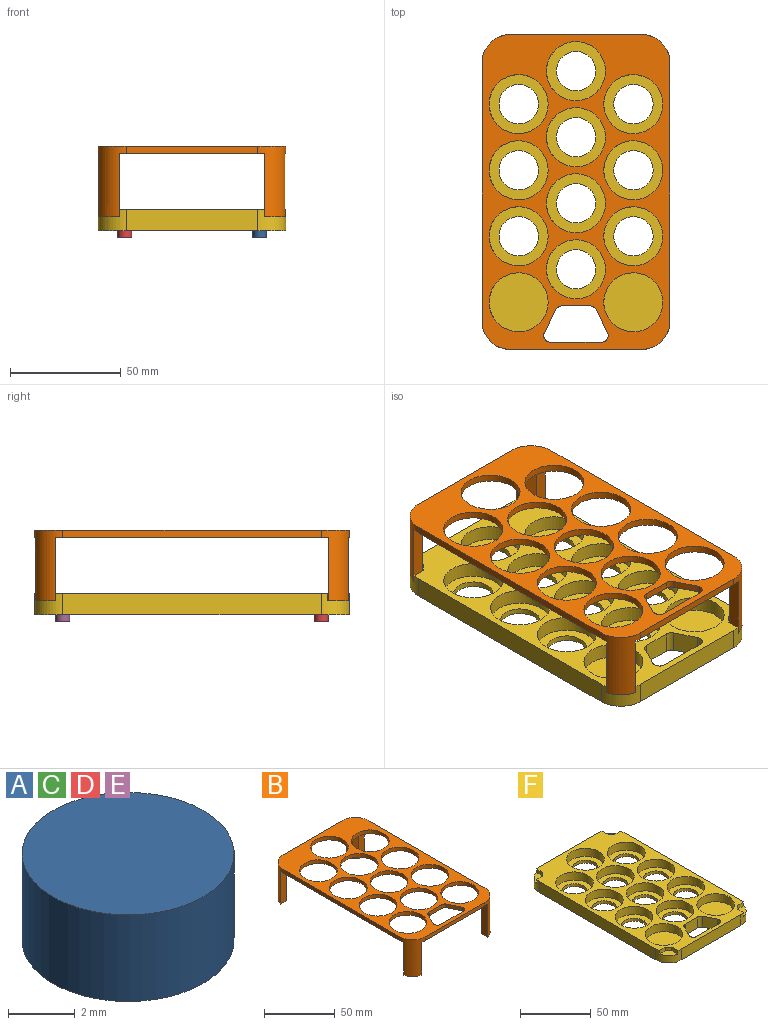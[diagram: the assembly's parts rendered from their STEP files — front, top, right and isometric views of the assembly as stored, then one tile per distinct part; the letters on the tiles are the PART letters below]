
ASSEMBLY  parts=6 mates=5
PART A: 3 faces, bbox 6.4x6.4x3.2 mm
  f0: cylinder r=3.17mm len=6.35mm, axis (0,0,-1), area 63.3mm2, adj f1,f2
  f1: plane 6.35x6.35mm, normal (0,0,1), area 31.7mm2, adj f0
  f2: plane 6.35x6.35mm, normal (0,0,-1), area 31.7mm2, adj f0
PART B: 46 faces, bbox 84.8x142.2x31.8 mm
  f0: plane 142.24x84.84mm, normal (0,0,-1), area 4623.7mm2, adj f4,f5,f6,f8,f9,f11,f12,f13
  f1: plane 142.24x84.84mm, normal (0,0,1), area 4829.7mm2, adj f4,f11,f12,f13,f18,f19,f20,f21
  f2: plane 9.12x9.12mm, normal (0,0,-1), area 51.5mm2, adj f8,f17,f39,f42
  f3: plane 9.12x9.12mm, normal (0,0,-1), area 51.5mm2, adj f9,f14,f38,f43
  f4: plane 116.84x3.18mm, normal (-1,0,0), area 371mm2, adj f0,f1,f39,f41
  f5: plane 28.58x5.82mm, normal (1,0,0), area 166.3mm2, adj f0,f7,f41,f44
  f6: plane 28.58x5.82mm, normal (-1,0,0), area 166.3mm2, adj f0,f10,f40,f45
  f7: plane 9.12x9.12mm, normal (0,0,-1), area 51.5mm2, adj f5,f16,f41,f44
  f8: plane 28.58x5.82mm, normal (1,0,0), area 166.3mm2, adj f0,f2,f39,f42
  f9: plane 28.58x5.82mm, normal (-1,0,0), area 166.3mm2, adj f0,f3,f38,f43
  f10: plane 9.12x9.12mm, normal (0,0,-1), area 51.5mm2, adj f6,f15,f40,f45
  f11: plane 116.84x3.18mm, normal (1,0,0), area 371mm2, adj f0,f1,f38,f40
  f12: plane 59.44x3.18mm, normal (0,-1,0), area 188.7mm2, adj f0,f1,f40,f41
  f13: plane 59.44x3.18mm, normal (0,1,0), area 188.7mm2, adj f0,f1,f38,f39
  f14: plane 28.58x5.82mm, normal (0,-1,0), area 166.3mm2, adj f0,f3,f38,f43
  f15: plane 28.58x5.82mm, normal (0,1,0), area 166.3mm2, adj f0,f10,f40,f45
  f16: plane 28.58x5.82mm, normal (0,1,0), area 166.3mm2, adj f0,f7,f41,f44
  f17: plane 28.58x5.82mm, normal (0,-1,0), area 166.3mm2, adj f0,f2,f39,f42
  f18: cylinder r=13.33mm len=26.67mm, axis (0,0,-1), area 266mm2, adj f0,f1
  f19: cylinder r=13.33mm len=26.67mm, axis (0,0,-1), area 266mm2, adj f0,f1
  f20: cylinder r=13.33mm len=26.67mm, axis (0,0,-1), area 266mm2, adj f0,f1
  f21: cylinder r=13.33mm len=26.67mm, axis (0,0,-1), area 266mm2, adj f0,f1
  f22: plane 10.16x5.09mm, normal (0.89,-0.45,0), area 36.1mm2, adj f0,f1,f23,f29
  f23: cylinder r=3.17mm len=4.6mm, axis (0,0,-1), area 20.5mm2, adj f0,f1,f22,f24
  f24: plane 22.74x3.18mm, normal (0,1,0), area 72.2mm2, adj f0,f1,f23,f25
  f25: cylinder r=3.17mm len=4.6mm, axis (0,0,-1), area 20.5mm2, adj f0,f1,f24,f26
  f26: plane 10.16x5.09mm, normal (-0.89,-0.45,0), area 36.1mm2, adj f0,f1,f25,f27
  f27: cylinder r=3.17mm len=3.18mm, axis (0,0,-1), area 11.2mm2, adj f0,f1,f26,f28
  f28: plane 12.55x3.18mm, normal (0,-1,0), area 39.9mm2, adj f0,f1,f27,f29
  f29: cylinder r=3.17mm len=3.18mm, axis (0,0,-1), area 11.2mm2, adj f0,f1,f22,f28
  f30: cylinder r=13.33mm len=26.67mm, axis (0,0,-1), area 266mm2, adj f0,f1
  f31: cylinder r=13.33mm len=26.67mm, axis (0,0,-1), area 266mm2, adj f0,f1
  f32: cylinder r=13.33mm len=26.67mm, axis (0,0,-1), area 266mm2, adj f0,f1
  f33: cylinder r=13.33mm len=26.67mm, axis (0,0,-1), area 266mm2, adj f0,f1
  f34: cylinder r=13.33mm len=26.67mm, axis (0,0,-1), area 266mm2, adj f0,f1
  f35: cylinder r=13.33mm len=26.67mm, axis (0,0,-1), area 266mm2, adj f0,f1
  f36: cylinder r=13.33mm len=26.67mm, axis (0,0,-1), area 266mm2, adj f0,f1
  f37: cylinder r=13.33mm len=26.67mm, axis (0,0,-1), area 266mm2, adj f0,f1
  f38: cylinder r=12.7mm len=31.75mm, axis (0,0,1), area 450mm2, adj f0,f1,f3,f9,f11,f13,f14
  f39: cylinder r=12.7mm len=31.75mm, axis (0,0,-1), area 450mm2, adj f0,f1,f2,f4,f8,f13,f17
  f40: cylinder r=12.7mm len=31.75mm, axis (0,0,-1), area 450mm2, adj f0,f1,f6,f10,f11,f12,f15
  f41: cylinder r=12.7mm len=31.75mm, axis (0,0,1), area 450mm2, adj f0,f1,f4,f5,f7,f12,f16
  f42: plane 28.58x3.3mm, normal (0.71,-0.71,0), area 133.4mm2, adj f0,f2,f8,f17
  f43: plane 28.58x3.3mm, normal (-0.71,-0.71,0), area 133.4mm2, adj f0,f3,f9,f14
  f44: plane 28.58x3.3mm, normal (0.71,0.71,0), area 133.4mm2, adj f0,f5,f7,f16
  f45: plane 28.58x3.3mm, normal (-0.71,0.71,0), area 133.4mm2, adj f0,f6,f10,f15
PART C: same geometry as A
PART D: same geometry as A
PART E: same geometry as A
PART F: 68 faces, bbox 84.8x142.2x9.5 mm
  f0: plane 142.24x84.84mm, normal (0,0,1), area 4614.4mm2, adj f1,f2,f3,f15,f16,f17,f18,f19
  f1: plane 116.84x9.53mm, normal (-1,0,0), area 1112.9mm2, adj f0,f14,f61,f63
  f2: plane 116.84x9.53mm, normal (1,0,0), area 1112.9mm2, adj f0,f14,f60,f62
  f3: plane 59.44x9.53mm, normal (0,-1,0), area 566.1mm2, adj f0,f14,f62,f63
  f4: cylinder r=8.89mm len=17.78mm, axis (0,0,1), area 141.9mm2, adj f14,f43
  f5: cylinder r=8.89mm len=17.78mm, axis (0,0,1), area 141.9mm2, adj f14,f41
  f6: cylinder r=8.89mm len=17.78mm, axis (0,0,1), area 141.9mm2, adj f14,f39
  f7: cylinder r=8.89mm len=17.78mm, axis (0,0,1), area 141.9mm2, adj f14,f37
  f8: cylinder r=8.89mm len=17.78mm, axis (0,0,1), area 141.9mm2, adj f14,f35
  f9: cylinder r=8.89mm len=17.78mm, axis (0,0,1), area 141.9mm2, adj f14,f33
  f10: cylinder r=8.89mm len=17.78mm, axis (0,0,1), area 141.9mm2, adj f14,f31
  f11: cylinder r=8.89mm len=17.78mm, axis (0,0,1), area 141.9mm2, adj f14,f29
  f12: cylinder r=8.89mm len=17.78mm, axis (0,0,1), area 141.9mm2, adj f14,f27
  f13: cylinder r=8.89mm len=17.78mm, axis (0,0,1), area 141.9mm2, adj f14,f25
  f14: plane 142.24x84.84mm, normal (0,0,-1), area 9050.6mm2, adj f1,f2,f3,f4,f5,f6,f7,f8
  f15: plane 59.44x9.53mm, normal (0,1,0), area 566.1mm2, adj f0,f14,f60,f61
  f16: plane 22.74x9.53mm, normal (0,1,0), area 216.6mm2, adj f0,f14,f17,f23
  f17: cylinder r=3.17mm len=9.53mm, axis (0,0,1), area 61.6mm2, adj f0,f14,f16,f18
  f18: plane 10.16x9.53mm, normal (-0.89,-0.45,0), area 108.2mm2, adj f0,f14,f17,f19
  f19: cylinder r=3.17mm len=9.53mm, axis (0,0,1), area 33.5mm2, adj f0,f14,f18,f20
  f20: plane 12.55x9.53mm, normal (0,-1,0), area 119.6mm2, adj f0,f14,f19,f21
  f21: cylinder r=3.17mm len=9.53mm, axis (0,0,1), area 33.5mm2, adj f0,f14,f20,f22
  f22: plane 10.16x9.53mm, normal (0.89,-0.45,0), area 108.2mm2, adj f0,f14,f21,f23
  f23: cylinder r=3.17mm len=9.53mm, axis (0,0,1), area 61.6mm2, adj f0,f14,f16,f22
  f24: cylinder r=13.33mm len=26.67mm, axis (0,0,1), area 585.2mm2, adj f0,f25
  f25: plane 26.67x26.67mm, normal (0,0,1), area 310.4mm2, adj f13,f24
  f26: cylinder r=13.33mm len=26.67mm, axis (0,0,1), area 585.2mm2, adj f0,f27
  f27: plane 26.67x26.67mm, normal (0,0,1), area 310.4mm2, adj f12,f26
  f28: cylinder r=13.33mm len=26.67mm, axis (0,0,1), area 585.2mm2, adj f0,f29
  f29: plane 26.67x26.67mm, normal (0,0,1), area 310.4mm2, adj f11,f28
  f30: cylinder r=13.33mm len=26.67mm, axis (0,0,1), area 585.2mm2, adj f0,f31
  f31: plane 26.67x26.67mm, normal (0,0,1), area 310.4mm2, adj f10,f30
  f32: cylinder r=13.33mm len=26.67mm, axis (0,0,1), area 585.2mm2, adj f0,f33
  f33: plane 26.67x26.67mm, normal (0,0,1), area 310.4mm2, adj f9,f32
  f34: cylinder r=13.33mm len=26.67mm, axis (0,0,1), area 585.2mm2, adj f0,f35
  f35: plane 26.67x26.67mm, normal (0,0,1), area 310.4mm2, adj f8,f34
  f36: cylinder r=13.33mm len=26.67mm, axis (0,0,1), area 585.2mm2, adj f0,f37
  f37: plane 26.67x26.67mm, normal (0,0,1), area 310.4mm2, adj f7,f36
  f38: cylinder r=13.33mm len=26.67mm, axis (0,0,1), area 585.2mm2, adj f0,f39
  f39: plane 26.67x26.67mm, normal (0,0,1), area 310.4mm2, adj f6,f38
  f40: cylinder r=13.33mm len=26.67mm, axis (0,0,1), area 585.2mm2, adj f0,f41
  f41: plane 26.67x26.67mm, normal (0,0,1), area 310.4mm2, adj f5,f40
  f42: cylinder r=13.33mm len=26.67mm, axis (0,0,1), area 585.2mm2, adj f0,f43
  f43: plane 26.67x26.67mm, normal (0,0,1), area 310.4mm2, adj f4,f42
  f44: cylinder r=13.33mm len=26.67mm, axis (0,0,1), area 585.2mm2, adj f0,f45
  f45: plane 26.67x26.67mm, normal (0,0,1), area 558.6mm2, adj f44
  f46: cylinder r=13.33mm len=26.67mm, axis (0,0,1), area 585.2mm2, adj f0,f47
  f47: plane 26.67x26.67mm, normal (0,0,1), area 558.6mm2, adj f46
  f48: plane 5.98x3.18mm, normal (0,1,0), area 19mm2, adj f0,f50,f61,f64
  f49: plane 5.98x3.18mm, normal (-1,0,0), area 19mm2, adj f0,f50,f61,f64
  f50: plane 9.28x9.28mm, normal (0,0,1), area 53.8mm2, adj f48,f49,f61,f64
  f51: plane 5.98x3.18mm, normal (1,0,0), area 19mm2, adj f0,f53,f60,f65
  f52: plane 5.98x3.18mm, normal (0,1,0), area 19mm2, adj f0,f53,f60,f65
  f53: plane 9.28x9.28mm, normal (0,0,1), area 53.8mm2, adj f51,f52,f60,f65
  f54: plane 5.98x3.18mm, normal (-1,0,0), area 19mm2, adj f0,f56,f63,f67
  f55: plane 5.98x3.18mm, normal (0,-1,0), area 19mm2, adj f0,f56,f63,f67
  f56: plane 9.28x9.28mm, normal (0,0,1), area 53.8mm2, adj f54,f55,f63,f67
  f57: plane 5.98x3.18mm, normal (0,-1,0), area 19mm2, adj f0,f59,f62,f66
  f58: plane 5.98x3.18mm, normal (1,0,0), area 19mm2, adj f0,f59,f62,f66
  f59: plane 9.28x9.28mm, normal (0,0,1), area 53.8mm2, adj f57,f58,f62,f66
  f60: cylinder r=12.7mm len=12.7mm, axis (0,0,1), area 146.2mm2, adj f0,f2,f14,f15,f51,f52,f53
  f61: cylinder r=12.7mm len=12.7mm, axis (0,0,-1), area 146.2mm2, adj f0,f1,f14,f15,f48,f49,f50
  f62: cylinder r=12.7mm len=12.7mm, axis (0,0,-1), area 146.2mm2, adj f0,f2,f3,f14,f57,f58,f59
  f63: cylinder r=12.7mm len=12.7mm, axis (0,0,1), area 146.2mm2, adj f0,f1,f3,f14,f54,f55,f56
  f64: plane 3.3x3.3mm, normal (-0.71,0.71,0), area 14.8mm2, adj f0,f48,f49,f50
  f65: plane 3.3x3.3mm, normal (0.71,0.71,0), area 14.8mm2, adj f0,f51,f52,f53
  f66: plane 3.3x3.3mm, normal (0.71,-0.71,0), area 14.8mm2, adj f0,f57,f58,f59
  f67: plane 3.3x3.3mm, normal (-0.71,-0.71,0), area 14.8mm2, adj f0,f54,f55,f56
PLACE A rot(axis=(-0.99,-0.11,0.08),0deg) t=(103.41,-181.6,-71.44)mm
PLACE B rot(axis=(-0.99,-0.11,0.08),0deg) t=(16.83,-22.34,-46.04)mm
PLACE C rot(axis=(-0.99,-0.11,0.08),0deg) t=(103.41,-64.76,-71.44)mm
PLACE D rot(axis=(-0.99,-0.11,0.08),0deg) t=(42.45,-181.6,-71.44)mm
PLACE E rot(axis=(-0.99,-0.11,0.08),0deg) t=(42.45,-64.76,-71.44)mm
PLACE F rot(axis=(-0.99,-0.11,0.08),0deg) t=(16.89,-22.28,-63.5)mm
MATE fastened E.f0 <-> F.f14  axis (0,0,1) through (-13.59,-35.04,-68.26)mm
MATE fastened D.f0 <-> F.f14  axis (0,0,1) through (-13.59,-151.88,-68.26)mm
MATE fastened B.f3 <-> F.f53  axis (0,0,-1) through (53.58,-28.01,-61.91)mm
MATE fastened A.f0 <-> F.f14  axis (0,0,1) through (47.37,-151.88,-68.26)mm
MATE fastened C.f0 <-> F.f14  axis (0,0,1) through (47.37,-35.04,-68.26)mm
